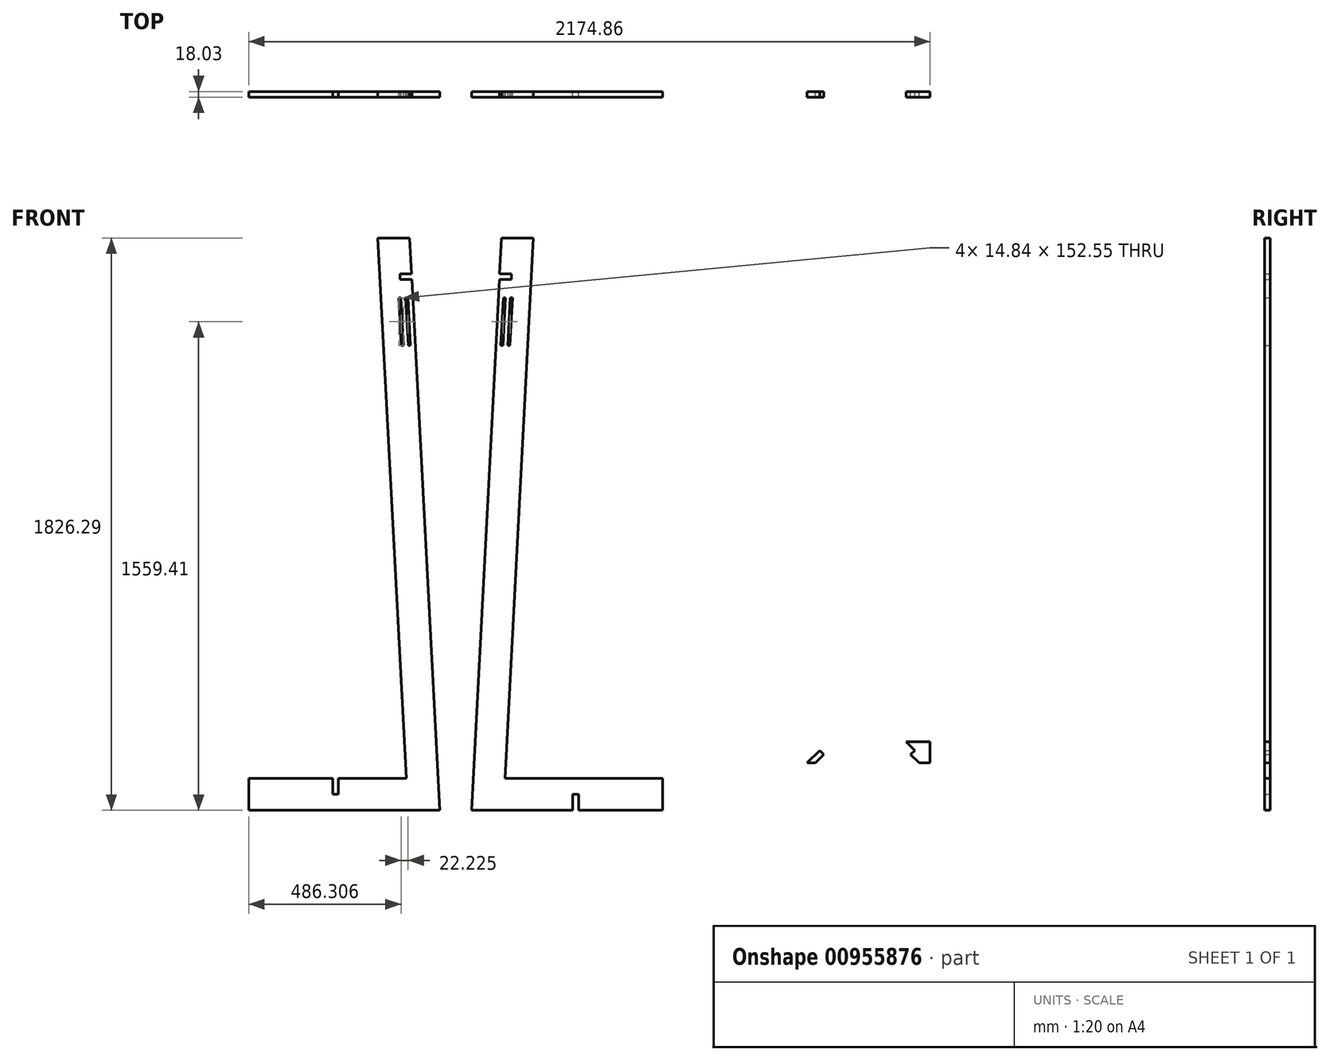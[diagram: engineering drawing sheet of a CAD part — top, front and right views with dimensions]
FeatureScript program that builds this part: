
annotation { "Feature Type Name" : "Feature", "Feature Type Description" : "" }
export const myFeature = defineFeature(function(context is Context, id is Id, definition is map)
    precondition{}
    {
        {
            var Q0;
            Q0=qCreatedBy(makeId("Front.planeOp"),FACE);
            var sketch = newSketch(context, id + "F0", { "sketchPlane" : qUnion([Q0])});
            skLineSegment(sketch, "E0", {"start": v(0, 0) * mm, "end": v(502.54, 0) * mm});
            skLineSegment(sketch, "E1", {"start": v(502.54, 0) * mm, "end": v(502.54, -101.6) * mm});
            skLineSegment(sketch, "E2", {"start": v(502.54, -101.6) * mm, "end": v(-107.06, -101.6) * mm});
            skLineSegment(sketch, "E3", {"start": v(-107.06, -101.6) * mm, "end": v(-11.35, 1724.7) * mm});
            skLineSegment(sketch, "E4", {"start": v(0, 0) * mm, "end": v(90.39, 1724.7) * mm});
            skLineSegment(sketch, "E5", {"start": v(90.39, 1724.7) * mm, "end": v(-11.35, 1724.7) * mm});
            skLineSegment(sketch, "E6.bottom", {"start": v(914.35, 0) * mm, "end": v(927.1, -12.75) * mm});
            skLineSegment(sketch, "E6.top", {"start": v(1345.4, 431.05) * mm, "end": v(1358.15, 418.3) * mm});
            skLineSegment(sketch, "E6.left", {"start": v(914.35, 0) * mm, "end": v(1345.4, 431.05) * mm});
            skLineSegment(sketch, "E6.right", {"start": v(927.1, -12.75) * mm, "end": v(1358.15, 418.3) * mm});
            skLineSegment(sketch, "E7", {"start": v(812.8, 0) * mm, "end": v(1498.6, 0) * mm, "construction": true});
            skLineSegment(sketch, "E8", {"start": v(1155.7, 0) * mm, "end": v(1155.7, -50.8) * mm, "construction": true});
            skLineSegment(sketch, "E9.MirrorCS", {"start": v(966, 431.05) * mm, "end": v(953.25, 418.3) * mm});
            skLineSegment(sketch, "E10.MirrorCS", {"start": v(1384.3, -12.75) * mm, "end": v(953.25, 418.3) * mm});
            skLineSegment(sketch, "E11.MirrorCS", {"start": v(1397.05, 0) * mm, "end": v(966, 431.05) * mm});
            skLineSegment(sketch, "E12.MirrorCS", {"start": v(1397.05, 0) * mm, "end": v(1384.3, -12.75) * mm});
            skLineSegment(sketch, "E13", {"start": v(1155.7, 215.85) * mm, "end": v(927.1, -12.75) * mm, "construction": true});
            skLineSegment(sketch, "E14", {"start": v(-107.06, -124.44) * mm, "end": v(216.23, -124.44) * mm, "construction": true});
            skPoint(sketch, "E15.oppositeSnap0", {"position": v(502.54, -50.8) * mm});
            skLineSegment(sketch, "E15.bottom", {"start": v(216.23, -101.6) * mm, "end": v(234.26, -101.6) * mm});
            skLineSegment(sketch, "E15.top", {"start": v(216.23, -50.8) * mm, "end": v(234.26, -50.8) * mm});
            skLineSegment(sketch, "E15.left", {"start": v(216.23, -101.6) * mm, "end": v(216.23, -50.8) * mm});
            skLineSegment(sketch, "E15.right", {"start": v(234.26, -101.6) * mm, "end": v(234.26, -50.8) * mm});
            skLineSegment(sketch, "E16", {"start": v(-157.86, -101.6) * mm, "end": v(-157.86, -50.8) * mm, "construction": true});
            skLineSegment(sketch, "E17.MirrorCS", {"start": v(-531.95, -101.6) * mm, "end": v(-549.99, -101.6) * mm, "construction": true});
            skLineSegment(sketch, "E18.MirrorCS", {"start": v(-531.95, -101.6) * mm, "end": v(-531.95, -50.8) * mm, "construction": true});
            skLineSegment(sketch, "E19.MirrorCS", {"start": v(-531.95, -50.8) * mm, "end": v(-549.99, -50.8) * mm});
            skLineSegment(sketch, "E20.MirrorCS", {"start": v(-549.99, -101.6) * mm, "end": v(-549.99, -50.8) * mm, "construction": true});
            skLineSegment(sketch, "E21.MirrorCS", {"start": v(-818.26, 0) * mm, "end": v(-818.26, -101.6) * mm});
            skLineSegment(sketch, "E22.MirrorCS", {"start": v(-315.73, 0) * mm, "end": v(-406.12, 1724.7) * mm});
            skLineSegment(sketch, "E23.MirrorCS", {"start": v(-208.66, -101.6) * mm, "end": v(-304.38, 1724.7) * mm});
            skLineSegment(sketch, "E24.MirrorCS", {"start": v(-315.73, 0) * mm, "end": v(-818.26, 0) * mm});
            skPoint(sketch, "E25.MirrorP", {"position": v(-818.26, -50.8) * mm});
            skLineSegment(sketch, "E26.MirrorCS", {"start": v(-406.12, 1724.7) * mm, "end": v(-304.38, 1724.7) * mm});
            skLineSegment(sketch, "E27.MirrorCS", {"start": v(-818.26, -101.6) * mm, "end": v(-208.66, -101.6) * mm});
            skLineSegment(sketch, "E28.MirrorCS", {"start": v(-531.95, 0) * mm, "end": v(-531.95, -50.8) * mm});
            skLineSegment(sketch, "E29.MirrorCS", {"start": v(-549.99, 0) * mm, "end": v(-549.99, -50.8) * mm});
            skLineSegment(sketch, "E30.MirrorCS", {"start": v(-531.95, 0) * mm, "end": v(-549.99, 0) * mm});
            skLineSegment(sketch, "E31.bottom", {"start": v(-18.29, 1592.36) * mm, "end": v(19.81, 1592.36) * mm});
            skLineSegment(sketch, "E31.top", {"start": v(-18.29, 1610.4) * mm, "end": v(19.81, 1610.4) * mm});
            skLineSegment(sketch, "E31.left", {"start": v(-18.29, 1592.36) * mm, "end": v(-18.29, 1610.4) * mm});
            skLineSegment(sketch, "E31.right", {"start": v(19.81, 1592.36) * mm, "end": v(19.81, 1610.4) * mm});
            skLineSegment(sketch, "E32.MirrorCS", {"start": v(-297.44, 1610.4) * mm, "end": v(-335.54, 1610.4) * mm});
            skLineSegment(sketch, "E33.MirrorCS", {"start": v(-335.54, 1592.36) * mm, "end": v(-335.54, 1610.4) * mm});
            skLineSegment(sketch, "E34.MirrorCS", {"start": v(-297.44, 1592.36) * mm, "end": v(-297.44, 1610.4) * mm});
            skLineSegment(sketch, "E35.MirrorCS", {"start": v(-297.44, 1592.36) * mm, "end": v(-335.54, 1592.36) * mm});
            skLineSegment(sketch, "E36", {"start": v(-18.29, 1592.36) * mm, "end": v(-18.29, -101.6) * mm, "construction": true});
            skLineSegment(sketch, "E37", {"start": v(-107.06, -101.6) * mm, "end": v(-18.29, -101.6) * mm, "construction": true});
            skLineSegment(sketch, "E38", {"start": v(920.72, -6.38) * mm, "end": v(983.5, 56.4) * mm, "construction": true});
            skLineSegment(sketch, "E39", {"start": v(983.5, 56.4) * mm, "end": v(977.12, 62.77) * mm});
            skLineSegment(sketch, "E40", {"start": v(983.5, 56.4) * mm, "end": v(989.87, 50.02) * mm});
            skLineSegment(sketch, "E41", {"start": v(983.5, 56.4) * mm, "end": v(1010.44, 83.34) * mm, "construction": true});
            skLineSegment(sketch, "E42", {"start": v(1010.44, 83.34) * mm, "end": v(1004.06, 89.72) * mm});
            skLineSegment(sketch, "E43", {"start": v(1004.06, 89.72) * mm, "end": v(1031, 116.66) * mm});
            skLineSegment(sketch, "E44", {"start": v(1031, 116.66) * mm, "end": v(954.8, 116.66) * mm});
            skLineSegment(sketch, "E45", {"start": v(954.8, 116.66) * mm, "end": v(954.8, 50.02) * mm});
            skLineSegment(sketch, "E46", {"start": v(954.8, 50.02) * mm, "end": v(1155.7, 50.02) * mm});
            skLineSegment(sketch, "E47", {"start": v(1010.44, 83.34) * mm, "end": v(1016.82, 76.96) * mm});
            skLineSegment(sketch, "E48", {"start": v(1016.82, 76.96) * mm, "end": v(1056.5, 116.66) * mm});
            skLineSegment(sketch, "E49", {"start": v(1056.5, 116.66) * mm, "end": v(1155.7, 116.66) * mm});
            skLineSegment(sketch, "E50.MirrorCS", {"start": v(1254.9, 116.66) * mm, "end": v(1155.7, 116.66) * mm});
            skLineSegment(sketch, "E51.MirrorCS", {"start": v(1356.6, 50.02) * mm, "end": v(1155.7, 50.02) * mm});
            skLineSegment(sketch, "E52.MirrorCS", {"start": v(1356.6, 116.66) * mm, "end": v(1356.6, 50.02) * mm});
            skLineSegment(sketch, "E53.MirrorCS", {"start": v(1280.4, 116.66) * mm, "end": v(1356.6, 116.66) * mm});
            skLineSegment(sketch, "E54.MirrorCS", {"start": v(1300.96, 83.34) * mm, "end": v(1294.58, 76.96) * mm});
            skLineSegment(sketch, "E55.MirrorCS", {"start": v(1300.96, 83.34) * mm, "end": v(1307.34, 89.72) * mm});
            skLineSegment(sketch, "E56.MirrorCS", {"start": v(1294.58, 76.96) * mm, "end": v(1254.9, 116.66) * mm});
            skLineSegment(sketch, "E57.MirrorCS", {"start": v(1307.34, 89.72) * mm, "end": v(1280.4, 116.66) * mm});
            skLineSegment(sketch, "E58", {"start": v(-5.44, 1534.09) * mm, "end": v(-13.42, 1381.9) * mm});
            skLineSegment(sketch, "E59", {"start": v(-13.42, 1381.9) * mm, "end": v(-6.57, 1381.54) * mm});
            skLineSegment(sketch, "E60", {"start": v(-6.57, 1381.54) * mm, "end": v(1.42, 1534.09) * mm});
            skLineSegment(sketch, "E61", {"start": v(1.42, 1534.09) * mm, "end": v(-5.44, 1534.09) * mm});
            skLineSegment(sketch, "E62", {"start": v(16.78, 1534.09) * mm, "end": v(8.8, 1381.9) * mm});
            skLineSegment(sketch, "E63", {"start": v(8.8, 1381.9) * mm, "end": v(15.65, 1381.54) * mm});
            skLineSegment(sketch, "E64", {"start": v(15.65, 1381.54) * mm, "end": v(23.65, 1534.09) * mm});
            skLineSegment(sketch, "E65", {"start": v(23.65, 1534.09) * mm, "end": v(16.78, 1534.09) * mm});
            skLineSegment(sketch, "E66.bottom", {"start": v(-50.1, 1470.7) * mm, "end": v(28.93, 1470.7) * mm});
            skLineSegment(sketch, "E66.top", {"start": v(-50.1, 1445.3) * mm, "end": v(28.93, 1445.3) * mm});
            skLineSegment(sketch, "E66.left", {"start": v(-50.1, 1470.7) * mm, "end": v(-50.1, 1445.3) * mm});
            skLineSegment(sketch, "E66.right", {"start": v(28.93, 1470.7) * mm, "end": v(28.93, 1445.3) * mm});
            skCircle(sketch, "E67", {"center": v(16.23, 1458) * mm, "radius": 3.43 * mm});
            skPoint(sketch, "E67.centerSnap0", {"position": v(28.93, 1458) * mm});
            skCircle(sketch, "E68", {"center": v(-6, 1458) * mm, "radius": 3.43 * mm});
            skPoint(sketch, "E69.endSnap0", {"position": v(-50.1, 1458) * mm});
            skLineSegment(sketch, "E70", {"start": v(-50.1, 1458) * mm, "end": v(-10.1, 1445.3) * mm});
            skPoint(sketch, "E71", {"position": v(-9.43, 1458) * mm});
            skLineSegment(sketch, "E72.MirrorCS", {"start": v(-310.28, 1534.09) * mm, "end": v(-302.3, 1381.9) * mm});
            skLineSegment(sketch, "E73.MirrorCS", {"start": v(-331.38, 1381.54) * mm, "end": v(-339.38, 1534.09) * mm});
            skLineSegment(sketch, "E74.MirrorCS", {"start": v(-339.38, 1534.09) * mm, "end": v(-332.5, 1534.09) * mm});
            skLineSegment(sketch, "E75.MirrorCS", {"start": v(-332.5, 1534.09) * mm, "end": v(-324.53, 1381.9) * mm});
            skLineSegment(sketch, "E76.MirrorCS", {"start": v(-309.16, 1381.54) * mm, "end": v(-317.15, 1534.09) * mm});
            skLineSegment(sketch, "E77.MirrorCS", {"start": v(-317.15, 1534.09) * mm, "end": v(-310.28, 1534.09) * mm});
            skLineSegment(sketch, "E78.MirrorCS", {"start": v(-302.3, 1381.9) * mm, "end": v(-309.16, 1381.54) * mm});
            skLineSegment(sketch, "E79.MirrorCS", {"start": v(-324.53, 1381.9) * mm, "end": v(-331.38, 1381.54) * mm});
            skLineSegment(sketch, "E80", {"start": v(39.52, 1724.7) * mm, "end": v(39.52, 1267.5) * mm});
            skLineSegment(sketch, "E81", {"start": v(39.52, 1267.5) * mm, "end": v(-65.62, 1267.5) * mm});
            skLineSegment(sketch, "E82", {"start": v(-5.44, 1534.09) * mm, "end": v(-19.42, 1267.5) * mm});
            skSolve(sketch);
        }
        {
            var Q0;
            Q0=makeQuery(id+"F0.imprint","IMPRINT",FACE,{"disambiguationData":[TD([[makeQuery(id+"F0.imprint","IMPRINT",EDGE,{"derivedFrom":sQuery(id+"F0.wireOp",EDGE,"E19.MirrorCS")}),1.0]])]});
            var Q1;
            Q1=makeQuery(id+"F0.imprint","IMPRINT",FACE,{"disambiguationData":[TD([[makeQuery(id+"F0.imprint","IMPRINT",EDGE,{"derivedFrom":sQuery(id+"F0.wireOp",EDGE,"E0")}),-1.0]])]});
            var Q2;
            {var subQ4=sQuery(id+"F0.wireOp",EDGE,"E6.bottom");Q2=makeQuery(id+"F0.imprint","IMPRINT",FACE,{"disambiguationData":[TD([[makeQuery(id+"F0.imprint","IMPRINT",EDGE,{"derivedFrom":subQ4}),-1.0]])]});}
            var Q3;
            {var subQ0=sQuery(id+"F0.wireOp",EDGE,"UBfg0rkv-vTGk-2FWx-0K6k-UeDQK5caFGxi");Q3=makeQuery(id+"F0.imprint","IMPRINT",FACE,{"disambiguationData":[TD([[makeQuery(id+"F0.imprint","IMPRINT",EDGE,{"derivedFrom":subQ0}),-1.0]])]});}
            var Q4;
            {var subQ4=sQuery(id+"F0.wireOp",EDGE,"E12.MirrorCS");Q4=makeQuery(id+"F0.imprint","IMPRINT",FACE,{"disambiguationData":[TD([[makeQuery(id+"F0.imprint","IMPRINT",EDGE,{"derivedFrom":subQ4}),1.0]])]});}
            var Q5;
            {var subQ0=sQuery(id+"F0.wireOp",EDGE,"E52.MirrorCS");Q5=makeQuery(id+"F0.imprint","IMPRINT",FACE,{"disambiguationData":[TD([[makeQuery(id+"F0.imprint","IMPRINT",EDGE,{"derivedFrom":subQ0}),-1.0]])]});}
            var Q6;
            {var subQ5=sQuery(id+"F0.wireOp",EDGE,"E54.MirrorCS");Q6=makeQuery(id+"F0.imprint","IMPRINT",FACE,{"disambiguationData":[TD([[makeQuery(id+"F0.imprint","IMPRINT",EDGE,{"derivedFrom":subQ5}),1.0]])]});}
            var Q7;
            {var subQ0=sQuery(id+"F0.wireOp",EDGE,"E48");Q7=makeQuery(id+"F0.imprint","IMPRINT",FACE,{"disambiguationData":[TD([[makeQuery(id+"F0.imprint","IMPRINT",EDGE,{"derivedFrom":subQ0}),-1.0]])]});}
            var Q8;
            {var subQ0=sQuery(id+"F0.wireOp",EDGE,"E43");Q8=makeQuery(id+"F0.imprint","IMPRINT",FACE,{"disambiguationData":[TD([[makeQuery(id+"F0.imprint","IMPRINT",EDGE,{"derivedFrom":subQ0}),1.0]])]});}
            var Q9;
            {var subQ3=sQuery(id+"F0.wireOp",EDGE,"E39");Q9=makeQuery(id+"F0.imprint","IMPRINT",FACE,{"disambiguationData":[TD([[makeQuery(id+"F0.imprint","IMPRINT",EDGE,{"derivedFrom":subQ3}),-1.0]])]});}
            var Q10;
            {var subQ0=sQuery(id+"F0.wireOp",EDGE,"E39");Q10=makeQuery(id+"F0.imprint","IMPRINT",FACE,{"disambiguationData":[TD([[makeQuery(id+"F0.imprint","IMPRINT",EDGE,{"derivedFrom":subQ0}),1.0]])]});}
            var Q11;
            {var subQ2=sQuery(id+"F0.wireOp",EDGE,"E66.top");var subQ6=sQuery(id+"F0.wireOp",EDGE,"E60");var subQ9=makeQuery(id+"F0.imprint","INTERSECT",VERTEX,{"derivedFrom":[subQ6,subQ2]});Q11=makeQuery(id+"F0.imprint","IMPRINT",FACE,{"disambiguationData":[TD([[makeQuery(id+"F0.imprint","IMPRINT",EDGE,{"disambiguationData":[TD([[subQ9,-1.0]])],"derivedFrom":subQ6}),-1.0]])]});}
            var Q12;
            {var subQ0=sQuery(id+"F0.wireOp",EDGE,"iL5P3PkR-sJst-Cz8f-bCPo-gTqLLt5mXmyN");var subQ1=sQuery(id+"F0.wireOp",EDGE,"E60");var subQ2=makeQuery(id+"F0.imprint","INTERSECT",VERTEX,{"derivedFrom":[subQ1,subQ0]});Q12=makeQuery(id+"F0.imprint","IMPRINT",FACE,{"disambiguationData":[TD([[makeQuery(id+"F0.imprint","IMPRINT",EDGE,{"disambiguationData":[TD([[subQ2,-1.0]])],"derivedFrom":subQ1}),-1.0]])]});}
            var Q13;
            {var subQ0=sQuery(id+"F0.wireOp",EDGE,"E66.top");var subQ1=sQuery(id+"F0.wireOp",EDGE,"E3");var subQ2=makeQuery(id+"F0.imprint","INTERSECT",VERTEX,{"derivedFrom":[subQ1,subQ0]});Q13=makeQuery(id+"F0.imprint","IMPRINT",FACE,{"disambiguationData":[TD([[makeQuery(id+"F0.imprint","IMPRINT",EDGE,{"disambiguationData":[TD([[subQ2,-1.0]])],"derivedFrom":subQ1}),-1.0]])]});}
            var Q14;
            {var subQ0=sQuery(id+"F0.wireOp",EDGE,"iL5P3PkR-sJst-Cz8f-bCPo-gTqLLt5mXmyN");var subQ1=sQuery(id+"F0.wireOp",EDGE,"E64");var subQ2=makeQuery(id+"F0.imprint","INTERSECT",VERTEX,{"derivedFrom":[subQ1,subQ0]});Q14=makeQuery(id+"F0.imprint","IMPRINT",FACE,{"disambiguationData":[TD([[makeQuery(id+"F0.imprint","IMPRINT",EDGE,{"disambiguationData":[TD([[subQ2,-1.0]])],"derivedFrom":subQ1}),-1.0]])]});}
            var Q15;
            {var subQ1=sQuery(id+"F0.wireOp",EDGE,"E66.top");var subQ3=sQuery(id+"F0.wireOp",EDGE,"E64");var subQ4=makeQuery(id+"F0.imprint","INTERSECT",VERTEX,{"derivedFrom":[subQ3,subQ1]});Q15=makeQuery(id+"F0.imprint","IMPRINT",FACE,{"disambiguationData":[TD([[makeQuery(id+"F0.imprint","IMPRINT",EDGE,{"disambiguationData":[TD([[subQ4,-1.0]])],"derivedFrom":subQ3}),-1.0]])]});}
            var Q16;
            {var subQ3=sQuery(id+"F0.wireOp",EDGE,"E3");var subQ5=sQuery(id+"F0.wireOp",EDGE,"E66.bottom");var subQ6=makeQuery(id+"F0.imprint","INTERSECT",VERTEX,{"derivedFrom":[subQ3,subQ5]});Q16=makeQuery(id+"F0.imprint","IMPRINT",FACE,{"disambiguationData":[TD([[makeQuery(id+"F0.imprint","IMPRINT",EDGE,{"disambiguationData":[TD([[subQ6,1.0]])],"derivedFrom":subQ3}),-1.0]])]});}
            var Q17;
            {var subQ17=sQuery(id+"F0.wireOp",EDGE,"E31.bottom");Q17=makeQuery(id+"F0.imprint","IMPRINT",FACE,{"disambiguationData":[TD([[makeQuery(id+"F0.imprint","IMPRINT",EDGE,{"derivedFrom":subQ17}),-1.0]])]});}
            var Q18;
            {var subQ4=sQuery(id+"F0.wireOp",EDGE,"E3");var subQ6=sQuery(id+"F0.wireOp",EDGE,"E81");var subQ8=makeQuery(id+"F0.imprint","INTERSECT",VERTEX,{"derivedFrom":[subQ4,subQ6]});Q18=makeQuery(id+"F0.imprint","IMPRINT",FACE,{"disambiguationData":[TD([[makeQuery(id+"F0.imprint","IMPRINT",EDGE,{"disambiguationData":[TD([[subQ8,-1.0]])],"derivedFrom":subQ4}),-1.0]])]});}
            extrude(context, id + "F1", {"entities" : qUnion([Q0, Q1, Q2, Q3, Q4, Q5, Q6, Q7, Q8, Q9, Q10, Q11, Q12, Q13, Q14, Q15, Q16, Q17, Q18]), "depth" : 18.03 * mm, "offsetDistance" : 25.4 * mm});
        }
    });
